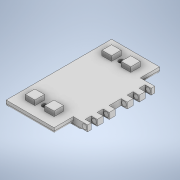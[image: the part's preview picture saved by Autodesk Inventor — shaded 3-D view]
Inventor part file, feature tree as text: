
AUTODESK INVENTOR PART (.ipt)
format: ipt  version: 2020 (Build 240168000, 168)  size: 698,880 bytes
history: native  units: in
note: dims shown in document units (in); Inventor stores cm internally (conversion verified against a paired STEP export)
features: extrude x10, sketch x10, fillet x4, mirror x2
ambient origin geometry x8: Origin, YZ Plane, XZ Plane, XY Plane, X Axis, Y Axis, Z Axis, Center Point
bodies: Solid1 (feature_tree)
feature tree (26):
  extrude  "Extrusion1"  Depth=1.5748in
  extrude  "Extrusion2"  Depth=0.315in
  extrude  "Extrusion3"  Depth=0.315in
  extrude  "Extrusion4"  Depth=0.1575in TaperAngle=0.0deg
  fillet  "Fillet1"  Radius=0.1575in
  fillet  "Fillet2"  Radius=0.1969in
  extrude  "Extrusion5"  Depth=0.1969in
  extrude  "Extrusion6"  Depth=0.0984in
  extrude  "Extrusion7"  Depth=0.2756in TaperAngle=0.0deg
  mirror  "Mirror1"
  fillet  "Fillet3"  Radius=0.1181in
  fillet  "Fillet4"  Radius=0.1969in
  extrude  "Extrusion8"  Depth=0.1969in
  extrude  "Extrusion9"  Depth=0.1575in
  extrude  "Extrusion10"  Depth=0.098in
  mirror  "Mirror2"
  sketch  "Sketch1"  dims[d0=1.5748in d1=3.4646in]
  sketch  "Sketch2"  dims[d2=0.1969in d3=0.0in d4=0.315in]
  sketch  "Sketch3"  dims[d5=0.315in d6=0.315in]
  sketch  "Sketch4"  dims[d7=0.315in d8=0.1575in d9=0.0in d10=0.1575in d11=0.1969in d12=0.0in]
  sketch  "Sketch5"  dims[d13=0.1969in d14=0.1969in]
  sketch  "Sketch6"  dims[d15=0.0984in d16=0.0in d17=0.0984in]
  sketch  "Sketch7"  dims[d18=0.0984in d19=0.2756in d20=0.0in d21=0.1181in d22=0.1969in]
  sketch  "Sketch8"  dims[d23=0.1969in d24=0.1969in]
  sketch  "Sketch9"  dims[d25=0.1969in d26=0.0in d27=0.1575in]
  sketch  "Sketch10"  dims[d28=0.3937in d29=0.7874in d30=0.0in d31=0.0in d32=0.098in d33=0.098in d34=0.7874in d35=90.0deg d36=0.4134in d37=1.1811in d38=1.1811in d39=0.1083in d40=0.1083in d43=0.8661in d44=0.4547in d45=1.2992in d46=1.2992in d47=0.1191in d48=0.1191in d49=0.9843in d50=0.6528in d51=0.6528in d52=1.378in d55=90.0deg d56=1.378in d57=3.1496in d58=2.3622in d59=2.3622in d60=0.189in d61=2.1654in d62=0.1811in d63=1.9685in d64=0.1693in d65=1.7717in d66=0.1575in d67=1.7717in d68=0.1476in d69=1.5748in d70=0.1398in d71=1.378in d72=0.135in d73=1.1811in d74=0.1329in d75=0.9843in d76=0.1331in d77=0.7874in d87=0.3937in d88=0.0515in d90=0.0984in d91=45.0deg d94=0.1181in d95=0.1476in d96=0.2953in d97=0.2362in d98=180.0deg d99=180.0deg d100=0.1969in d101=0.1969in d102=0.3937in d103=0.0412in d104=2.3622in d105=0.3937in d106=0.0412in d107=2.3622in d108=0.0787in d109=45.0deg d110=0.0413in d111=0.0787in d112=45.0deg d113=0.0413in d114=0.2756in d115=0.3937in d116=0.0in d117=0.3937in d118=0.0in d119=0.3543in d120=0.0412in d121=2.3622in d122=0.3543in d123=0.0412in d124=2.3622in d125=0.0591in d126=45.0deg d127=0.0311in d128=0.0591in d129=45.0deg d130=0.0311in d131=0.2756in d132=0.1181in d133=0.0in d134=0.7874in d135=90.0deg d136=0.4134in d137=1.1811in d138=1.1811in d139=0.1083in d140=0.1083in d141=0.8661in d142=0.4547in d143=1.2992in d144=1.2992in d145=0.9843in d146=0.6528in d147=0.6528in d148=90.0deg d149=3.1496in d150=2.3622in d151=2.3622in d152=0.189in d153=2.1654in d154=0.1811in d155=1.9685in d156=0.1693in d157=1.7717in d158=0.1575in d159=1.7717in d160=0.1476in d161=1.5748in d162=0.1398in d163=1.378in d164=0.135in d165=1.1811in d166=0.1329in d167=0.9843in d168=0.1331in d169=0.7874in d170=0.3937in d171=0.0515in d172=0.0984in d173=45.0deg d174=0.1181in d175=0.1476in d176=0.2953in d177=0.2362in d178=180.0deg d179=180.0deg d180=0.1969in d181=0.1969in d182=0.3937in d183=0.0412in d184=2.3622in d185=0.3937in d186=0.0412in d187=2.3622in d188=0.0787in d189=45.0deg d190=0.0413in d191=0.0787in d192=45.0deg d193=0.0413in d194=0.2756in d195=0.3937in d196=0.0in d197=0.3937in d198=0.0in d199=0.3543in d200=0.0412in d201=2.3622in d202=0.3543in d203=0.0412in d204=2.3622in d205=0.0591in d206=45.0deg d207=0.0311in d208=0.0591in d209=45.0deg d210=0.0311in d211=0.2756in d212=0.0787in d213=0.0in d214=0.7874in d215=90.0deg d216=0.4134in d217=1.1811in d218=1.1811in d219=0.1083in d220=0.1083in d221=0.8661in d222=0.4547in d223=1.2992in d224=1.2992in d225=0.9843in d226=0.6528in d227=0.6528in d228=90.0deg d229=3.1496in d230=2.3622in d231=2.3622in d232=0.189in d233=2.1654in d234=0.1811in d235=1.9685in d236=0.1693in d237=1.7717in d238=0.1575in d239=1.7717in d240=0.1476in d241=1.5748in d242=0.1398in d243=1.378in d244=0.135in d245=1.1811in d246=0.1329in d247=0.9843in d248=0.1331in d249=0.7874in d250=0.3937in d251=0.0515in d252=0.0984in d253=45.0deg d254=0.1181in d255=0.1476in d256=0.2953in d257=0.2362in d258=180.0deg d259=180.0deg d260=0.1969in d261=0.1969in d262=0.3937in d263=0.0412in d264=2.3622in d265=0.3937in d266=0.0412in d267=2.3622in d268=0.0787in d269=45.0deg d270=0.0413in d271=0.0787in d272=45.0deg d273=0.0413in d274=0.2756in d275=0.3937in d276=0.0in d277=0.3937in d278=0.0in d279=0.3543in d280=0.0412in d281=2.3622in d282=0.3543in d283=0.0412in d284=2.3622in d285=0.0591in d286=45.0deg d287=0.0311in d288=0.0591in d289=45.0deg d290=0.0311in d291=0.2756in d292=0.0591in d293=0.0in]
